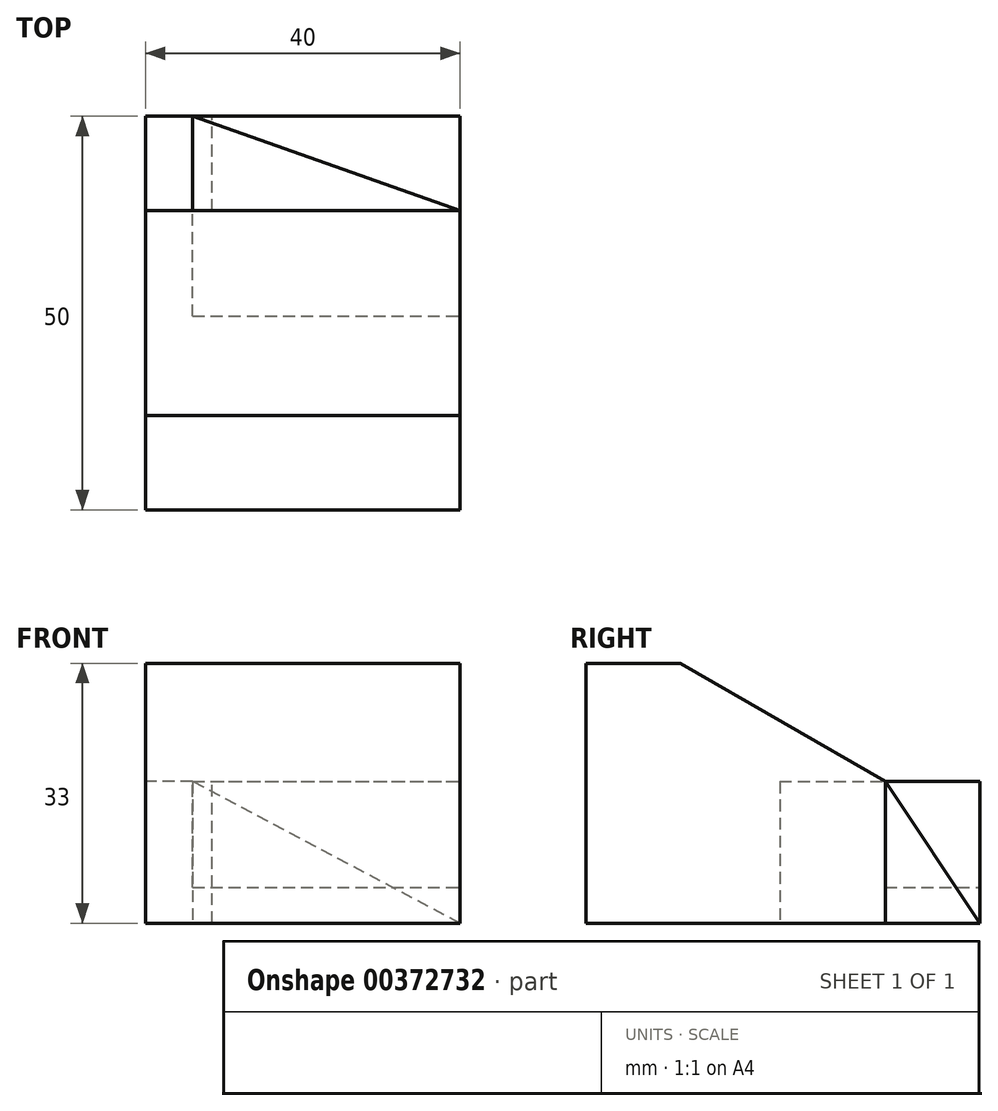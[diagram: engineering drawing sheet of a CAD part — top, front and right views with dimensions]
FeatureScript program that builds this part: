
annotation { "Feature Type Name" : "Feature", "Feature Type Description" : "" }
export const myFeature = defineFeature(function(context is Context, id is Id, definition is map)
    precondition{}
    {
        {
            var Q0;
            Q0=qCreatedBy(makeId("Right.planeOp"),FACE);
            var sketch = newSketch(context, id + "F0", { "sketchPlane" : qUnion([Q0])});
            skLineSegment(sketch, "E0", {"start": v(14.5, -35.53) * mm, "end": v(-23.5, -35.53) * mm});
            skLineSegment(sketch, "E1", {"start": v(-23.5, -35.53) * mm, "end": v(-23.5, -2.53) * mm});
            skLineSegment(sketch, "E2", {"start": v(-23.5, -2.53) * mm, "end": v(-11.5, -2.53) * mm});
            skLineSegment(sketch, "E3", {"start": v(14.5, -35.53) * mm, "end": v(14.5, -17.53) * mm});
            skLineSegment(sketch, "E4", {"start": v(14.5, -17.53) * mm, "end": v(-11.5, -2.53) * mm});
            skSolve(sketch);
        }
        {
            var Q0;
            Q0=makeQuery(id+"F0.imprint","IMPRINT",FACE,{"disambiguationData":[TD([[makeQuery(id+"F0.imprint","IMPRINT",EDGE,{"derivedFrom":sQuery(id+"F0.wireOp",EDGE,"E0")}),-1.0]])]});
            extrude(context, id + "F1", {"entities" : qUnion([Q0]), "depth" : 40 * mm});
        }
        {
            var Q0;
            Q0=makeQuery(id+"F1.opExtrude","CAP_FACE",FACE,{"disambiguationData":[OSD([sQuery(id+"F0.wireOp",EDGE,"E0"),sQuery(id+"F0.wireOp",EDGE,"E1"),sQuery(id+"F0.wireOp",EDGE,"E2"),sQuery(id+"F0.wireOp",EDGE,"E3"),sQuery(id+"F0.wireOp",EDGE,"E4")])],"isStart":true});
            var sketch = newSketch(context, id + "F2", { "sketchPlane" : qUnion([Q0])});
            skLineSegment(sketch, "E5", {"start": v(-14.5, -17.53) * mm, "end": v(-26.5, -17.53) * mm});
            skLineSegment(sketch, "E6", {"start": v(-26.5, -17.53) * mm, "end": v(-26.5, -35.53) * mm});
            skLineSegment(sketch, "E7", {"start": v(-26.5, -35.53) * mm, "end": v(-14.5, -35.53) * mm});
            skLineSegment(sketch, "E8", {"start": v(-14.5, -35.53) * mm, "end": v(-14.5, -17.53) * mm});
            skSolve(sketch);
        }
        {
            var Q0;
            Q0=makeQuery(id+"F2.imprint","IMPRINT",FACE,{"disambiguationData":[TD([[makeQuery(id+"F2.imprint","IMPRINT",EDGE,{"derivedFrom":sQuery(id+"F2.wireOp",EDGE,"E5")}),1.0]])]});
            extrude(context, id + "F3", {"entities" : qUnion([Q0]), "operationType" : NewBodyOperationType.ADD, "oppositeDirection" : true, "depth" : 6 * mm});
        }
        {
            var Q0;
            Q0=makeQuery(id+"F3.opExtrude","SWEPT_FACE",FACE,{"disambiguationData":[OSD([sQuery(id+"F2.wireOp",EDGE,"E5")])]});
            var sketch = newSketch(context, id + "F4", { "sketchPlane" : qUnion([Q0])});
            skLineSegment(sketch, "E9", {"start": v(6, 14.5) * mm, "end": v(40, 14.5) * mm});
            skLineSegment(sketch, "E10", {"start": v(40, 14.5) * mm, "end": v(6, 26.5) * mm});
            skLineSegment(sketch, "E11", {"start": v(6, 26.5) * mm, "end": v(6, 14.5) * mm});
            skSolve(sketch);
        }
        {
            var Q0;
            Q0=makeQuery(id+"F3.opExtrude","SWEPT_FACE",FACE,{"disambiguationData":[OSD([sQuery(id+"F2.wireOp",EDGE,"E6")])]});
            var sketch = newSketch(context, id + "F5", { "sketchPlane" : qUnion([Q0])});
            skLineSegment(sketch, "E12", {"start": v(0, -35.53) * mm, "end": v(-40, -35.53) * mm});
            skLineSegment(sketch, "E13", {"start": v(-40, -35.53) * mm, "end": v(-6, -17.53) * mm});
            skLineSegment(sketch, "E14", {"start": v(-6, -17.53) * mm, "end": v(0, -17.53) * mm});
            skSolve(sketch);
        }
        {
            var Q0;
            Q0=makeQuery(id+"F1.opExtrude","CAP_FACE",FACE,{"disambiguationData":[OSD([sQuery(id+"F0.wireOp",EDGE,"E0"),sQuery(id+"F0.wireOp",EDGE,"E1"),sQuery(id+"F0.wireOp",EDGE,"E2"),sQuery(id+"F0.wireOp",EDGE,"E3"),sQuery(id+"F0.wireOp",EDGE,"E4")])],"isStart":false});
            var sketch = newSketch(context, id + "F6", { "sketchPlane" : qUnion([Q0])});
            skLineSegment(sketch, "E15", {"start": v(14.5, -35.53) * mm, "end": v(26.5, -35.53) * mm});
            skLineSegment(sketch, "E16", {"start": v(26.5, -35.53) * mm, "end": v(14.5, -17.53) * mm});
            skLineSegment(sketch, "E17", {"start": v(14.5, -17.53) * mm, "end": v(14.5, -35.53) * mm});
            skSolve(sketch);
        }
        {
            var Q0;
            {var subQ2=sQuery(id+"F5.wireOp",EDGE,"E13");Q0=makeQuery(id+"F5.imprint","IMPRINT",FACE,{"disambiguationData":[TD([[makeQuery(id+"F5.imprint","IMPRINT",EDGE,{"derivedFrom":subQ2}),-1.0]])]});}
            extrude(context, id + "F7", {"entities" : qUnion([Q0]), "oppositeDirection" : true, "depth" : 25.4 * mm});
        }
        {
            var Q0;
            Q0=makeQuery(id+"F4.imprint","IMPRINT",FACE,{"disambiguationData":[TD([[makeQuery(id+"F4.imprint","IMPRINT",EDGE,{"derivedFrom":sQuery(id+"F4.wireOp",EDGE,"E9")}),1.0]])]});
            extrude(context, id + "F8", {"entities" : qUnion([Q0]), "oppositeDirection" : true, "depth" : 13.46 * mm});
        }
        {
            var Q0;
            Q0=makeQuery(id+"F6.imprint","IMPRINT",FACE,{"disambiguationData":[TD([[makeQuery(id+"F6.imprint","IMPRINT",EDGE,{"derivedFrom":sQuery(id+"F6.wireOp",EDGE,"E15")}),1.0]])]});
            extrude(context, id + "F9", {"entities" : qUnion([Q0]), "oppositeDirection" : true, "depth" : 31.5 * mm});
        }
    });
